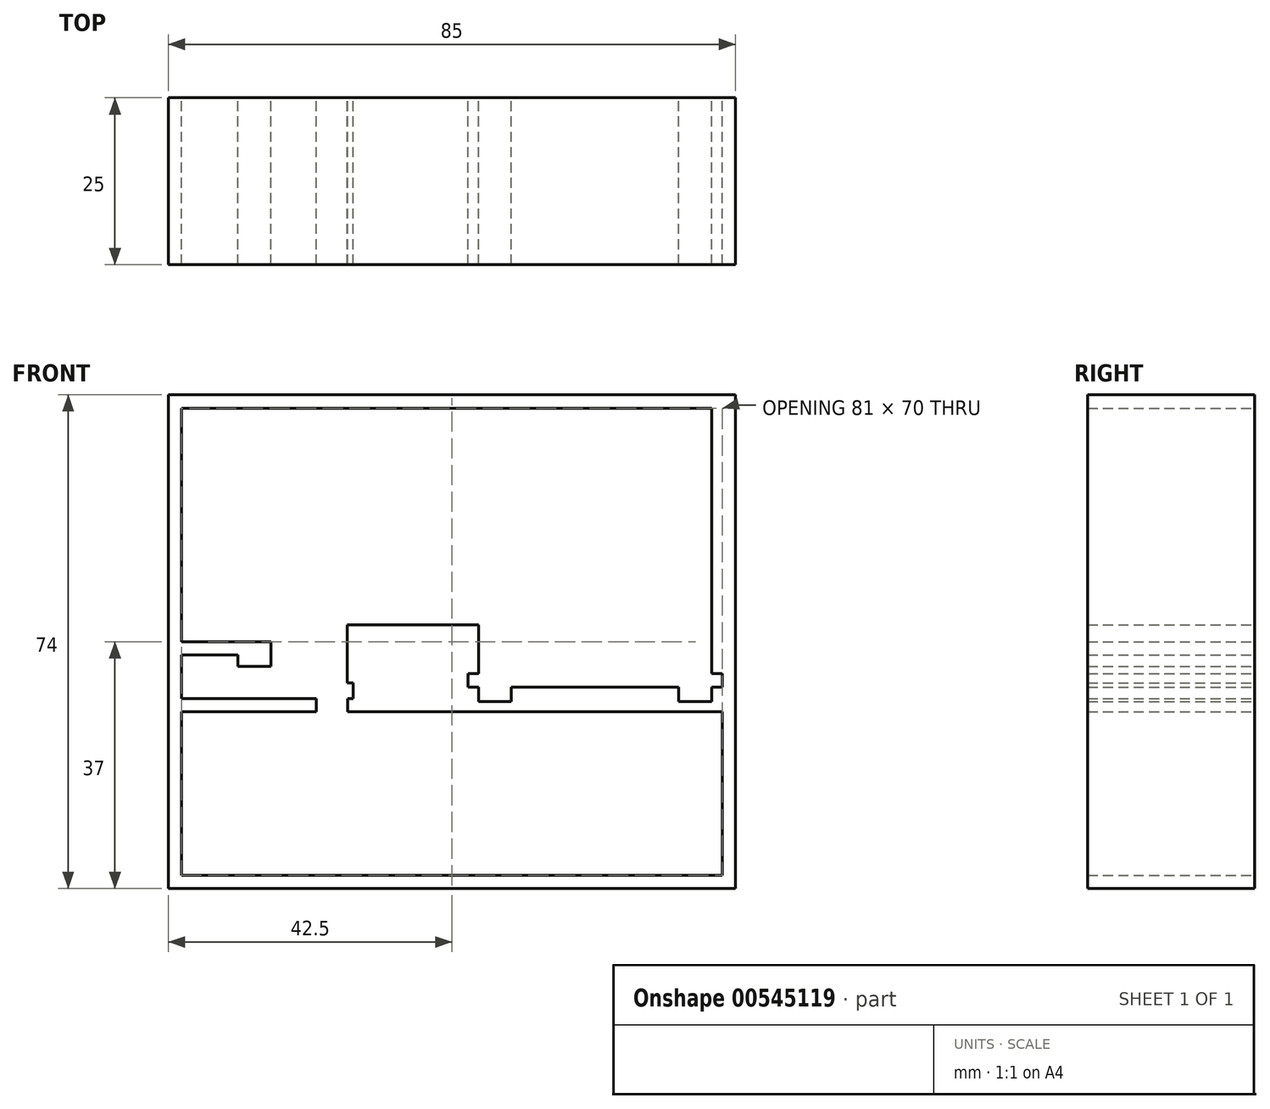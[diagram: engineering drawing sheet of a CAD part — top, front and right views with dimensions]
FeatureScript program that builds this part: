
annotation { "Feature Type Name" : "Feature", "Feature Type Description" : "" }
export const myFeature = defineFeature(function(context is Context, id is Id, definition is map)
    precondition{}
    {
        {
            var Q0;
            Q0=qCreatedBy(makeId("Front.planeOp"),FACE);
            var sketch = newSketch(context, id + "F0", { "sketchPlane" : qUnion([Q0])});
            skLineSegment(sketch, "E0.bottom", {"start": v(-42.5, 0) * mm, "end": v(42.5, 0) * mm});
            skLineSegment(sketch, "E0.top", {"start": v(-42.5, 74) * mm, "end": v(42.5, 74) * mm});
            skLineSegment(sketch, "E0.left", {"start": v(-42.5, 0) * mm, "end": v(-42.5, 74) * mm});
            skLineSegment(sketch, "E0.right", {"start": v(42.5, 0) * mm, "end": v(42.5, 74) * mm});
            skLineSegment(sketch, "E1", {"start": v(-40.5, 2) * mm, "end": v(-40.5, 26.5) * mm});
            skLineSegment(sketch, "E2", {"start": v(-40.5, 26.5) * mm, "end": v(-20.3, 26.5) * mm});
            skLineSegment(sketch, "E3", {"start": v(-20.3, 26.5) * mm, "end": v(-20.3, 28.5) * mm});
            skLineSegment(sketch, "E4", {"start": v(-20.3, 28.5) * mm, "end": v(-40.5, 28.5) * mm});
            skLineSegment(sketch, "E5", {"start": v(-40.5, 28.5) * mm, "end": v(-40.5, 35) * mm});
            skLineSegment(sketch, "E6", {"start": v(-27.1, 37) * mm, "end": v(-27.1, 33.3) * mm});
            skLineSegment(sketch, "E7", {"start": v(38.9, 32.2) * mm, "end": v(40.5, 32.2) * mm});
            skLineSegment(sketch, "E8", {"start": v(40.5, 32.2) * mm, "end": v(40.5, 30.2) * mm});
            skLineSegment(sketch, "E9", {"start": v(40.5, 30.2) * mm, "end": v(38.9, 30.2) * mm});
            skLineSegment(sketch, "E10", {"start": v(38.9, 30.2) * mm, "end": v(38.9, 28) * mm});
            skLineSegment(sketch, "E11", {"start": v(38.9, 28) * mm, "end": v(34, 28) * mm});
            skLineSegment(sketch, "E12", {"start": v(34, 28) * mm, "end": v(34, 30.2) * mm});
            skLineSegment(sketch, "E13", {"start": v(34, 30.2) * mm, "end": v(8.9, 30.2) * mm});
            skLineSegment(sketch, "E14", {"start": v(-15.7, 39.5) * mm, "end": v(4, 39.5) * mm});
            skLineSegment(sketch, "E15", {"start": v(-14.8, 28.5) * mm, "end": v(-15.6, 28.5) * mm});
            skLineSegment(sketch, "E16", {"start": v(-15.6, 28.5) * mm, "end": v(-15.6, 26.5) * mm});
            skLineSegment(sketch, "E17", {"start": v(-15.6, 26.5) * mm, "end": v(40.5, 26.5) * mm});
            skLineSegment(sketch, "E18", {"start": v(40.5, 26.5) * mm, "end": v(40.5, 2) * mm});
            skLineSegment(sketch, "E19", {"start": v(40.5, 2) * mm, "end": v(-40.5, 2) * mm});
            skLineSegment(sketch, "E20", {"start": v(-40.3, 28.6) * mm, "end": v(-40.3, 30.5) * mm, "construction": true});
            skLineSegment(sketch, "E21", {"start": v(-40.3, 30.5) * mm, "end": v(-41.3, 30.5) * mm, "construction": true});
            skLineSegment(sketch, "E22", {"start": v(-41.3, 30.5) * mm, "end": v(-41.3, 34.5) * mm, "construction": true});
            skLineSegment(sketch, "E23", {"start": v(-41.3, 34.5) * mm, "end": v(-32.3, 34.5) * mm, "construction": true});
            skLineSegment(sketch, "E24", {"start": v(-32.3, 34.5) * mm, "end": v(-32.3, 33.1) * mm, "construction": true});
            skLineSegment(sketch, "E25", {"start": v(-32.3, 33.1) * mm, "end": v(-19.8, 33.1) * mm, "construction": true});
            skLineSegment(sketch, "E26", {"start": v(-19.8, 33.1) * mm, "end": v(-19.8, 33.6) * mm, "construction": true});
            skLineSegment(sketch, "E27", {"start": v(-19.8, 33.6) * mm, "end": v(-15.8, 33.6) * mm, "construction": true});
            skLineSegment(sketch, "E28", {"start": v(-15.8, 26.6) * mm, "end": v(-19.8, 26.6) * mm, "construction": true});
            skLineSegment(sketch, "E29", {"start": v(-19.8, 26.6) * mm, "end": v(-19.8, 28.6) * mm, "construction": true});
            skLineSegment(sketch, "E30", {"start": v(-19.8, 28.6) * mm, "end": v(-40.3, 28.6) * mm, "construction": true});
            skLineSegment(sketch, "E31", {"start": v(-15.8, 26.6) * mm, "end": v(-15.8, 28.6) * mm, "construction": true});
            skLineSegment(sketch, "E32", {"start": v(-15.8, 28.6) * mm, "end": v(-15.3, 28.6) * mm, "construction": true});
            skLineSegment(sketch, "E33", {"start": v(-40.5, 35) * mm, "end": v(-32.1, 35) * mm});
            skLineSegment(sketch, "E34", {"start": v(-32.1, 35) * mm, "end": v(-32.1, 33.3) * mm});
            skLineSegment(sketch, "E35", {"start": v(-32.1, 33.3) * mm, "end": v(-27.1, 33.3) * mm});
            skLineSegment(sketch, "E36", {"start": v(-15.3, 28.6) * mm, "end": v(-15.3, 30.6) * mm, "construction": true});
            skLineSegment(sketch, "E37", {"start": v(-15.3, 30.6) * mm, "end": v(-15.8, 30.6) * mm, "construction": true});
            skLineSegment(sketch, "E38", {"start": v(-15.8, 30.6) * mm, "end": v(-15.8, 33.6) * mm, "construction": true});
            skLineSegment(sketch, "E39.bottom", {"start": v(-38.5, 2.5) * mm, "end": v(38.5, 2.5) * mm, "construction": true});
            skLineSegment(sketch, "E39.top", {"start": v(-38.5, 24.5) * mm, "end": v(38.5, 24.5) * mm, "construction": true});
            skLineSegment(sketch, "E39.left", {"start": v(-38.5, 2.5) * mm, "end": v(-38.5, 24.5) * mm, "construction": true});
            skLineSegment(sketch, "E39.right", {"start": v(38.5, 2.5) * mm, "end": v(38.5, 24.5) * mm, "construction": true});
            skLineSegment(sketch, "E40", {"start": v(-14.8, 28.5) * mm, "end": v(-14.8, 30.8) * mm});
            skLineSegment(sketch, "E41", {"start": v(-14.8, 30.8) * mm, "end": v(-15.7, 30.8) * mm});
            skLineSegment(sketch, "E42", {"start": v(-15.7, 30.8) * mm, "end": v(-15.7, 39.5) * mm});
            skLineSegment(sketch, "E43", {"start": v(2.7, 30.5) * mm, "end": v(4.2, 30.5) * mm, "construction": true});
            skLineSegment(sketch, "E44", {"start": v(4.2, 30.5) * mm, "end": v(4.2, 28.5) * mm, "construction": true});
            skLineSegment(sketch, "E45", {"start": v(4.2, 28.5) * mm, "end": v(8.7, 28.5) * mm, "construction": true});
            skLineSegment(sketch, "E46", {"start": v(8.7, 28.5) * mm, "end": v(8.7, 30.5) * mm, "construction": true});
            skLineSegment(sketch, "E47", {"start": v(8.7, 30.5) * mm, "end": v(34.2, 30.5) * mm, "construction": true});
            skLineSegment(sketch, "E48", {"start": v(34.2, 30.5) * mm, "end": v(34.2, 28.5) * mm, "construction": true});
            skLineSegment(sketch, "E49", {"start": v(34.2, 28.5) * mm, "end": v(38.7, 28.5) * mm, "construction": true});
            skLineSegment(sketch, "E50", {"start": v(38.7, 28.5) * mm, "end": v(38.7, 30.5) * mm, "construction": true});
            skLineSegment(sketch, "E51", {"start": v(38.7, 30.5) * mm, "end": v(40.2, 30.5) * mm, "construction": true});
            skLineSegment(sketch, "E52", {"start": v(40.2, 30.5) * mm, "end": v(40.2, 32) * mm, "construction": true});
            skLineSegment(sketch, "E53", {"start": v(40.2, 32) * mm, "end": v(38.7, 32) * mm, "construction": true});
            skLineSegment(sketch, "E54", {"start": v(38.7, 32) * mm, "end": v(38.7, 37.5) * mm, "construction": true});
            skLineSegment(sketch, "E55", {"start": v(38.7, 37.5) * mm, "end": v(4.2, 37.5) * mm, "construction": true});
            skLineSegment(sketch, "E56", {"start": v(4.2, 37.5) * mm, "end": v(4.2, 32) * mm, "construction": true});
            skLineSegment(sketch, "E57", {"start": v(4.2, 32) * mm, "end": v(2.7, 32) * mm, "construction": true});
            skLineSegment(sketch, "E58", {"start": v(2.7, 32) * mm, "end": v(2.7, 30.5) * mm, "construction": true});
            skLineSegment(sketch, "E59", {"start": v(8.9, 30.2) * mm, "end": v(8.9, 28) * mm});
            skLineSegment(sketch, "E60", {"start": v(8.9, 28) * mm, "end": v(4, 28) * mm});
            skLineSegment(sketch, "E61", {"start": v(4, 28) * mm, "end": v(4, 30.2) * mm});
            skLineSegment(sketch, "E62", {"start": v(4, 30.2) * mm, "end": v(2.4, 30.2) * mm});
            skLineSegment(sketch, "E63", {"start": v(2.4, 30.2) * mm, "end": v(2.4, 32.2) * mm});
            skLineSegment(sketch, "E64", {"start": v(2.4, 32.2) * mm, "end": v(4, 32.2) * mm});
            skLineSegment(sketch, "E65", {"start": v(4, 32.2) * mm, "end": v(4, 39.5) * mm});
            skLineSegment(sketch, "E66", {"start": v(38.9, 32.2) * mm, "end": v(38.9, 72) * mm});
            skLineSegment(sketch, "E67", {"start": v(27.7, 70) * mm, "end": v(27.7, 67) * mm, "construction": true});
            skLineSegment(sketch, "E68", {"start": v(27.7, 67) * mm, "end": v(23.7, 67) * mm, "construction": true});
            skLineSegment(sketch, "E69", {"start": v(23.7, 67) * mm, "end": v(23.7, 57) * mm, "construction": true});
            skLineSegment(sketch, "E70", {"start": v(23.7, 57) * mm, "end": v(27.7, 57) * mm, "construction": true});
            skLineSegment(sketch, "E71", {"start": v(27.7, 57) * mm, "end": v(27.7, 53.5) * mm, "construction": true});
            skLineSegment(sketch, "E72", {"start": v(27.7, 53.5) * mm, "end": v(36.7, 53.5) * mm, "construction": true});
            skLineSegment(sketch, "E73", {"start": v(36.7, 53.5) * mm, "end": v(36.7, 45.5) * mm, "construction": true});
            skLineSegment(sketch, "E74", {"start": v(36.7, 45.5) * mm, "end": v(38.7, 45.5) * mm, "construction": true});
            skLineSegment(sketch, "E75", {"start": v(38.7, 45.5) * mm, "end": v(38.7, 57.5) * mm, "construction": true});
            skLineSegment(sketch, "E76", {"start": v(60.7, 57.5) * mm, "end": v(60.7, 64.5) * mm, "construction": true});
            skLineSegment(sketch, "E77", {"start": v(60.7, 64.5) * mm, "end": v(38.7, 64.5) * mm, "construction": true});
            skLineSegment(sketch, "E78", {"start": v(38.7, 64.5) * mm, "end": v(38.7, 70) * mm, "construction": true});
            skLineSegment(sketch, "E79", {"start": v(38.7, 70) * mm, "end": v(27.7, 70) * mm, "construction": true});
            skLineSegment(sketch, "E80", {"start": v(38.7, 57.5) * mm, "end": v(60.7, 57.5) * mm, "construction": true});
            skLineSegment(sketch, "E81", {"start": v(-27.1, 37) * mm, "end": v(-40.5, 37) * mm});
            skLineSegment(sketch, "E82", {"start": v(-40.5, 37) * mm, "end": v(-40.5, 72) * mm});
            skLineSegment(sketch, "E83", {"start": v(-40.5, 72) * mm, "end": v(38.9, 72) * mm});
            skSolve(sketch);
        }
        {
            var Q0;
            Q0=makeQuery(id+"F0.imprint","IMPRINT",FACE,{"disambiguationData":[TD([[makeQuery(id+"F0.imprint","IMPRINT",EDGE,{"derivedFrom":sQuery(id+"F0.wireOp",EDGE,"E0.bottom")}),1.0]])]});
            extrude(context, id + "F1", {"entities" : qUnion([Q0]), "depth" : 25 * mm, "offsetDistance" : 25 * mm});
        }
    });
